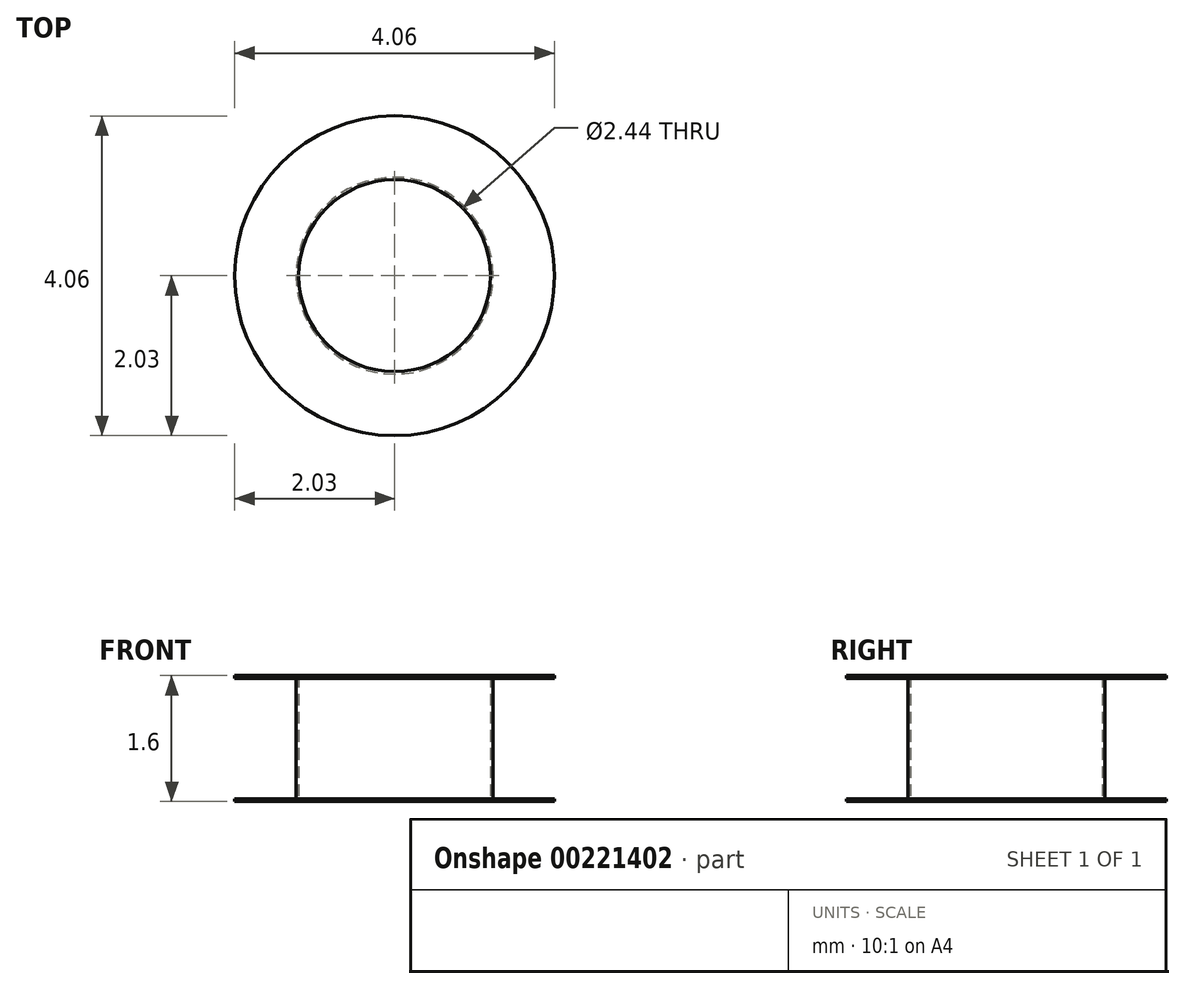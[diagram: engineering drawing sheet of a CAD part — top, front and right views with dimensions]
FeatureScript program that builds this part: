
annotation { "Feature Type Name" : "Feature", "Feature Type Description" : "" }
export const myFeature = defineFeature(function(context is Context, id is Id, definition is map)
    precondition{}
    {
        {
            var Q0;
            Q0=qCreatedBy(makeId("Top.planeOp"),FACE);
            var sketch = newSketch(context, id + "F0", { "sketchPlane" : qUnion([Q0])});
            skCircle(sketch, "E0", {"center": v(0, 0) * mm, "radius": 2.03 * mm});
            skSolve(sketch);
        }
        {
            var Q0;
            Q0=makeQuery(id+"F0.imprint","IMPRINT",FACE,{"disambiguationData":[TD([[makeQuery(id+"F0.imprint","IMPRINT",EDGE,{"derivedFrom":sQuery(id+"F0.wireOp",EDGE,"E0")}),1.0]])]});
            extrude(context, id + "F1", {"entities" : qUnion([Q0]), "depth" : 0.04 * mm});
        }
        {
            var Q0;
            Q0=makeQuery(id+"F1.opExtrude","CAP_FACE",FACE,{"disambiguationData":[OSD([sQuery(id+"F0.wireOp",EDGE,"E0")])],"isStart":false});
            var sketch = newSketch(context, id + "F2", { "sketchPlane" : qUnion([Q0])});
            skCircle(sketch, "E1", {"center": v(0, 0) * mm, "radius": 1.25 * mm});
            skSolve(sketch);
        }
        {
            var Q0;
            Q0=makeQuery(id+"F2.imprint","IMPRINT",FACE,{"disambiguationData":[TD([[makeQuery(id+"F2.imprint","IMPRINT",EDGE,{"derivedFrom":sQuery(id+"F2.wireOp",EDGE,"E1")}),1.0]])]});
            extrude(context, id + "F3", {"entities" : qUnion([Q0]), "operationType" : NewBodyOperationType.ADD, "depth" : 1.53 * mm});
        }
        {
            var Q0;
            Q0=makeQuery(id+"F3.opExtrude","CAP_FACE",FACE,{"disambiguationData":[OSD([sQuery(id+"F2.wireOp",EDGE,"E1")])],"isStart":false});
            var sketch = newSketch(context, id + "F4", { "sketchPlane" : qUnion([Q0])});
            skCircle(sketch, "E2.0", {"center": v(0, 0) * mm, "radius": 2.03 * mm});
            skSolve(sketch);
        }
        {
            var Q0;
            Q0 = qSketchRegion(id + "F4", true);
            extrude(context, id + "F5", {"entities" : qUnion([Q0]), "operationType" : NewBodyOperationType.ADD, "depth" : 0.04 * mm});
        }
        {
            var Q0;
            Q0=qCreatedBy(makeId("Top.planeOp"),FACE);
            var sketch = newSketch(context, id + "F6", { "sketchPlane" : qUnion([Q0])});
            skCircle(sketch, "E3", {"center": v(0, 0) * mm, "radius": 1.22 * mm});
            skSolve(sketch);
        }
        {
            var Q0;
            Q0 = qSketchRegion(id + "F6", true);
            extrude(context, id + "F7", {"entities" : qUnion([Q0]), "operationType" : NewBodyOperationType.REMOVE, "endBound" : BoundingType.THROUGH_ALL, "depth" : 25 * mm});
        }
    });
